# Revit family: Hand_Dryer-Automatic-American_Dryers-EXT_Series
name_source: partatom
category: Specialty Equipment
revit_build: Autodesk Revit 2015 (Build: 20140606_1530(x64)
units: mm (PartAtom-declared; Revit-internal decimal feet)

## types (1)
- 7
    Amperage = 0 A
    Amperage Range = 4.5 A to 2.3 A
    BIMobject category = Dryers (Hand & Hair)
    BIMobject category code = sanitary-hand-and-hair-dryers
    BIMobject main category = Sanitary
    BIMobject main category code = sanitary
    Back Offset = 1/8"
    Brand url = http://worlddryer.com
    Case Material = Plastic-American Dryer-Flame Retardant White ABS
    Default Elevation = 0"
    Description = Extreme Air®, high speed hand dryer series.
    Design country = United States
    Edition number = 1
    Installation instructions = https://www.americandryer.com
    Manufacturer = American Dryer
    Manufacturer Fax = 734.421.5580
    Manufacturer country = United States
    Manufacturer name = World Dryer
    Material main = Steel
    Model = EXT7
    Nominal height = 0"
    Nominal width = 0"
    Number of Poles = 1
    OmniClass Code = 23-31 25 15
    OmniClass Description = Hand Dryers
    Power Factor = 1
    Product Documentation Link = http://184.168.180.225
    Product Guid = 5f9eb826-d76b-4158-a706-59365dd51237
    Product Page URL = http://americandryer.com
    Product SKU = hand-dryer-world-dryer-ext-series
    Product certification = https://www.americandryer.com
    Product data url = https://bimobject.com
    Product family = Hand and Hair Dryers
    Product group = Extreme Air®
    Product url = http://www.americandryer.com
    QR code = http://bimobject.com
    Recessed Offset = 0"
    Technical description = https://www.americandryer.com
    URL = http://www.americandryer.com
    Uniclass 2.0 Code = PR-02-03
    Uniclass 2.0 Description = Air Dryers
    Uniclass 2015 Code = Pr_40_20_76
    Uniclass 2015 Name = Sanitary accessories
    Void Offset = 1/8"
    Voltage = 0 V
    Voltage Range = 100 V to 240 V
    Watts = 540 W
    Weight Net (Kg) = 0
    With Recessed Mount = No
    With Splash Guard = No
    With Universal Adapter Plate = No

## geometry (parser evidence)
native form markers: Blend x10, Sweep x4
no freeform markers — native parametric forms only
